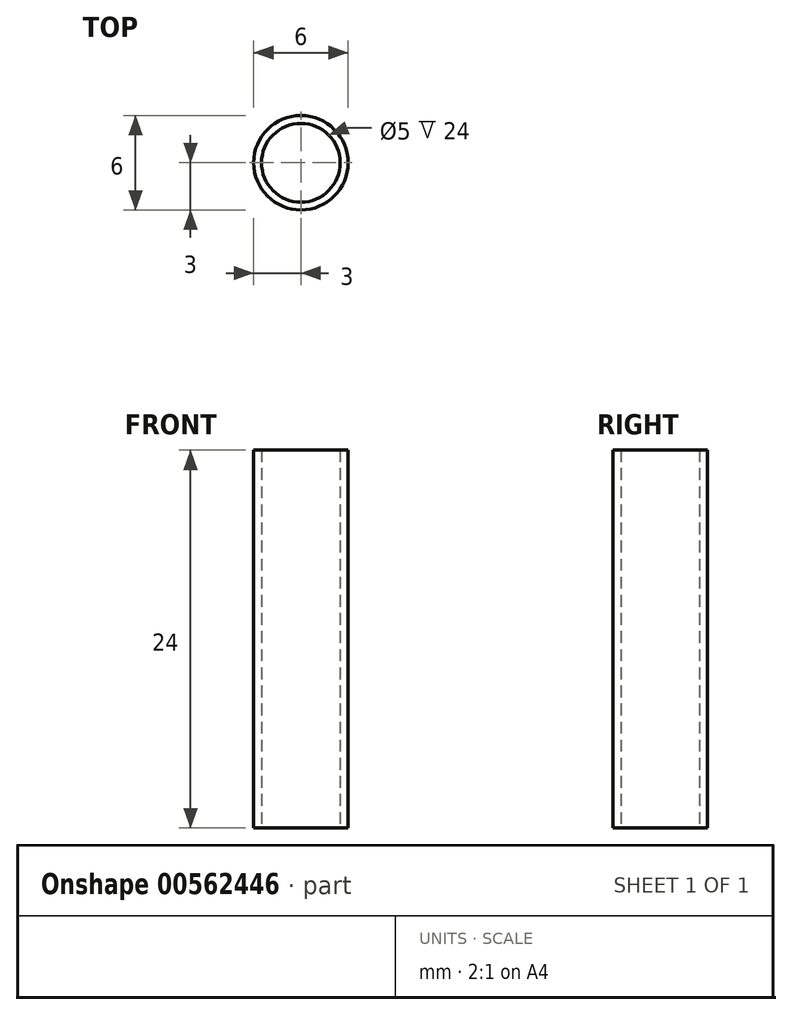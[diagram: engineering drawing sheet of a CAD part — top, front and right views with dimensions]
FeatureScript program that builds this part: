
annotation { "Feature Type Name" : "Feature", "Feature Type Description" : "" }
export const myFeature = defineFeature(function(context is Context, id is Id, definition is map)
    precondition{}
    {
        {
            var Q0;
            Q0=qCreatedBy(makeId("Top.planeOp"),FACE);
            var sketch = newSketch(context, id + "F0", { "sketchPlane" : qUnion([Q0])});
            skLineSegment(sketch, "E0.rect.bottom", {"start": v(-28.11, 28.11) * mm, "end": v(28.12, 28.11) * mm});
            skLineSegment(sketch, "E0.rect.top", {"start": v(-28.11, -28.11) * mm, "end": v(28.11, -28.11) * mm});
            skLineSegment(sketch, "E0.rect.left", {"start": v(-28.11, 28.12) * mm, "end": v(-28.12, -28.11) * mm});
            skLineSegment(sketch, "E0.rect.right", {"start": v(28.12, 28.12) * mm, "end": v(28.11, -28.11) * mm});
            skPoint(sketch, "E0.rect.middle", {"position": v(0, 0) * mm});
            skCircle(sketch, "E1", {"center": v(0, 0) * mm, "radius": 19.04 * mm});
            skCircle(sketch, "E2", {"center": v(0, 0) * mm, "radius": 3.98 * mm});
            skCircle(sketch, "E3", {"center": v(-23.62, 23.62) * mm, "radius": 2.5 * mm});
            skCircle(sketch, "E4", {"center": v(23.62, 23.62) * mm, "radius": 2.5 * mm});
            skCircle(sketch, "E5", {"center": v(23.62, -23.62) * mm, "radius": 2.5 * mm});
            skCircle(sketch, "E6", {"center": v(-23.62, -23.62) * mm, "radius": 2.5 * mm});
            skLineSegment(sketch, "E7.rect.bottom", {"start": v(-23.62, 23.62) * mm, "end": v(23.62, 23.62) * mm, "construction": true});
            skLineSegment(sketch, "E7.rect.top", {"start": v(-23.62, -23.62) * mm, "end": v(23.62, -23.62) * mm, "construction": true});
            skLineSegment(sketch, "E7.rect.left", {"start": v(-23.62, 23.62) * mm, "end": v(-23.62, -23.62) * mm, "construction": true});
            skLineSegment(sketch, "E7.rect.right", {"start": v(23.62, 23.62) * mm, "end": v(23.62, -23.62) * mm, "construction": true});
            skCircle(sketch, "E8", {"center": v(0, 0) * mm, "radius": 5.38 * mm});
            skCircle(sketch, "E9", {"center": v(-25.37, 0) * mm, "radius": 8.13 * mm});
            skCircle(sketch, "E10", {"center": v(25.37, 0) * mm, "radius": 8.13 * mm});
            skCircle(sketch, "E11", {"center": v(0, -25.37) * mm, "radius": 8.13 * mm});
            skCircle(sketch, "E12", {"center": v(-25.37, 0) * mm, "radius": 3.42 * mm});
            skCircle(sketch, "E13", {"center": v(25.37, 0) * mm, "radius": 3.41 * mm});
            skCircle(sketch, "E14", {"center": v(0, -25.37) * mm, "radius": 3.42 * mm});
            skCircle(sketch, "E15", {"center": v(-23.62, 23.62) * mm, "radius": 3 * mm});
            skSolve(sketch);
        }
        {
            var Q0;
            Q0=makeQuery(id+"F0.imprint","IMPRINT",FACE,{"disambiguationData":[TD([[makeQuery(id+"F0.imprint","IMPRINT",EDGE,{"derivedFrom":sQuery(id+"F0.wireOp",EDGE,"E3")}),-1.0]])]});
            extrude(context, id + "F1", {"entities" : qUnion([Q0]), "depth" : 24 * mm});
        }
    });
